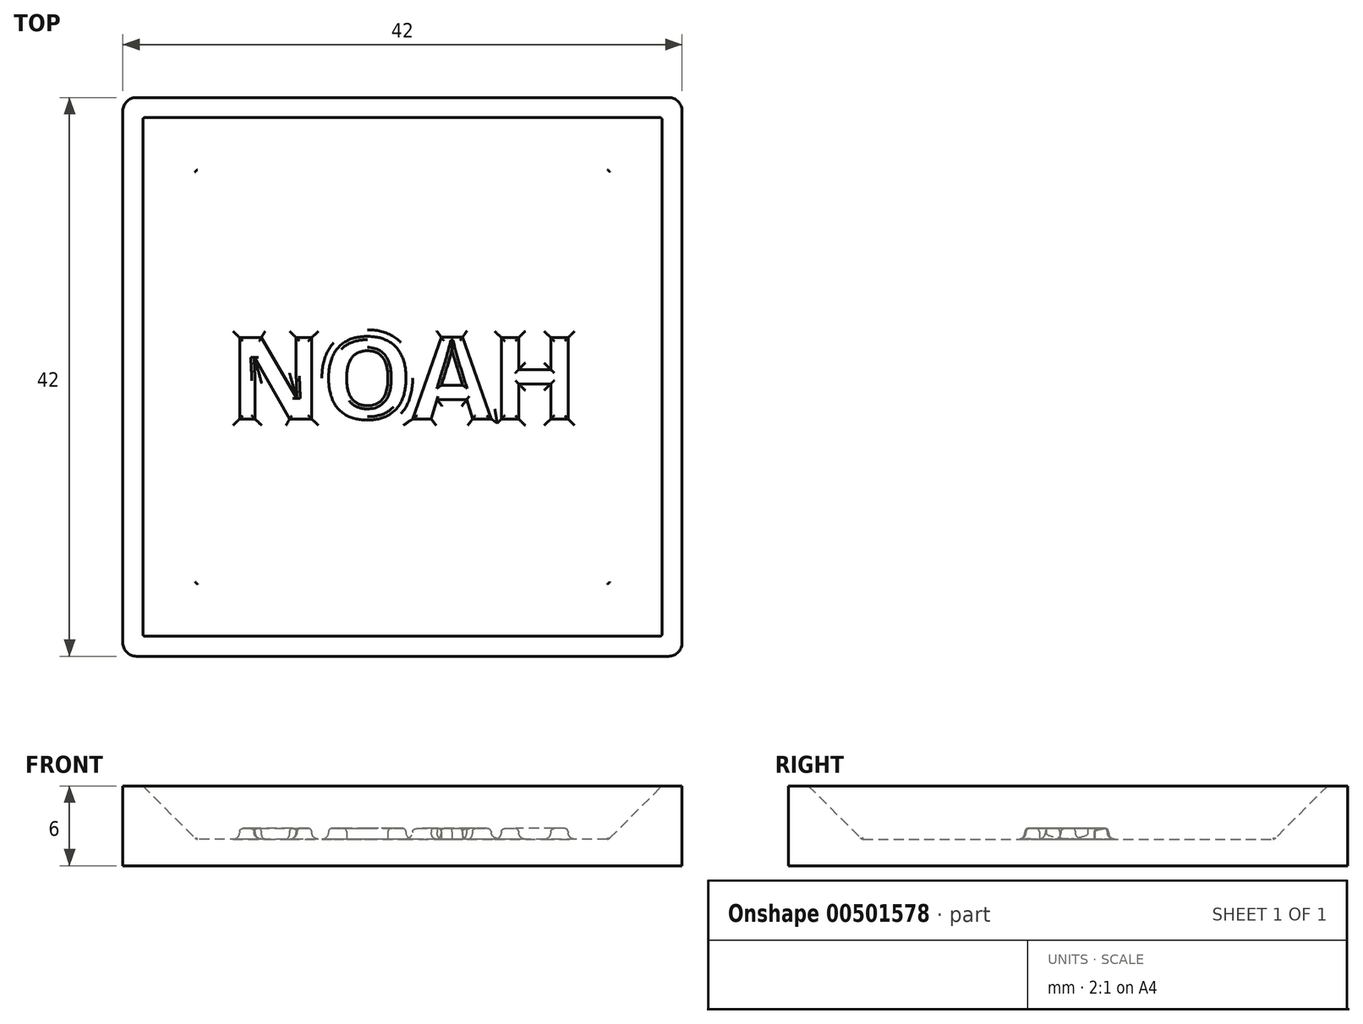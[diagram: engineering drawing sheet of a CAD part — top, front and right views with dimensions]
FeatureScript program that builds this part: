
annotation { "Feature Type Name" : "Feature", "Feature Type Description" : "" }
export const myFeature = defineFeature(function(context is Context, id is Id, definition is map)
    precondition{}
    {
        {
            var Q0;
            Q0=qCreatedBy(makeId("Top.planeOp"),FACE);
            var sketch = newSketch(context, id + "F0", { "sketchPlane" : qUnion([Q0])});
            skLineSegment(sketch, "E0.bottom", {"start": v(-21, 21) * mm, "end": v(21, 21) * mm});
            skLineSegment(sketch, "E0.top", {"start": v(-21, -21) * mm, "end": v(21, -21) * mm});
            skLineSegment(sketch, "E0.left", {"start": v(-21, 21) * mm, "end": v(-21, -21) * mm});
            skLineSegment(sketch, "E0.right", {"start": v(21, 21) * mm, "end": v(21, -21) * mm});
            skSolve(sketch);
        }
        {
            var Q0;
            Q0=qSketchRegion(id+"F0",true);
            extrude(context, id + "F1", {"entities" : qUnion([Q0]), "depth" : 2 * mm});
        }
        {
            var Q0;
            Q0=makeQuery(id+"F1.opExtrude","CAP_FACE",FACE,{"disambiguationData":[OSD([sQuery(id+"F0.wireOp",EDGE,"E0.bottom"),sQuery(id+"F0.wireOp",EDGE,"E0.top"),sQuery(id+"F0.wireOp",EDGE,"E0.left"),sQuery(id+"F0.wireOp",EDGE,"E0.right")])],"isStart":false});
            var sketch = newSketch(context, id + "F2", { "sketchPlane" : qUnion([Q0])});
            skLineSegment(sketch, "E1.bottom", {"start": v(-21, 21) * mm, "end": v(21, 21) * mm});
            skLineSegment(sketch, "E1.top", {"start": v(-21, -21) * mm, "end": v(21, -21) * mm});
            skLineSegment(sketch, "E1.left", {"start": v(-21, 21) * mm, "end": v(-21, -21) * mm});
            skLineSegment(sketch, "E1.right", {"start": v(21, 21) * mm, "end": v(21, -21) * mm});
            skLineSegment(sketch, "E2.bottom", {"start": v(-15.5, 15.5) * mm, "end": v(15.5, 15.5) * mm});
            skLineSegment(sketch, "E2.top", {"start": v(-15.5, -15.5) * mm, "end": v(15.5, -15.5) * mm});
            skLineSegment(sketch, "E2.left", {"start": v(-15.5, 15.5) * mm, "end": v(-15.5, -15.5) * mm});
            skLineSegment(sketch, "E2.right", {"start": v(15.5, 15.5) * mm, "end": v(15.5, -15.5) * mm});
            skSolve(sketch);
        }
        {
            var Q0;
            Q0=qSketchRegion(id+"F2",true);
            extrude(context, id + "F3", {"entities" : qUnion([Q0]), "operationType" : NewBodyOperationType.ADD, "depth" : 4 * mm});
        }
        {
            var Q0;
            Q0=makeQuery(id+"F3.opExtrude","CAP_EDGE",EDGE,{"disambiguationData":[OSD([sQuery(id+"F2.wireOp",EDGE,"E2.left")])],"isStart":false});
            var Q1;
            Q1=makeQuery(id+"F3.opExtrude","CAP_EDGE",EDGE,{"disambiguationData":[OSD([sQuery(id+"F2.wireOp",EDGE,"E2.bottom")])],"isStart":false});
            var Q2;
            Q2=makeQuery(id+"F3.opExtrude","CAP_EDGE",EDGE,{"disambiguationData":[OSD([sQuery(id+"F2.wireOp",EDGE,"E2.right")])],"isStart":false});
            var Q3;
            Q3=makeQuery(id+"F3.opExtrude","CAP_EDGE",EDGE,{"disambiguationData":[OSD([sQuery(id+"F2.wireOp",EDGE,"E2.top")])],"isStart":false});
            chamfer(context, id + "F4", {"entities" : qUnion([Q0, Q1, Q2, Q3]), "width" : 4 * mm, "tangentPropagation" : true});
        }
        {
            var Q0;
            Q0=makeQuery(id+"F1.opExtrude","CAP_FACE",FACE,{"disambiguationData":[OSD([sQuery(id+"F0.wireOp",EDGE,"E0.bottom"),sQuery(id+"F0.wireOp",EDGE,"E0.top"),sQuery(id+"F0.wireOp",EDGE,"E0.left"),sQuery(id+"F0.wireOp",EDGE,"E0.right")])],"isStart":false});
            var sketch = newSketch(context, id + "F5", { "sketchPlane" : qUnion([Q0])});
            skText(sketch, "E3", { "text": "NOAH", "fontName": "OpenSans-Bold.ttf"});
            const initialGuessF5  = {"E3": [-0.013, -0.00316, 1, 0, 0.00616]};
            skSetInitialGuess(sketch, initialGuessF5);
            skSolve(sketch);
        }
        {
            var Q0;
            Q0 = qSketchRegion(id + "F5", true);
            extrude(context, id + "F6", {"entities" : qUnion([Q0]), "operationType" : NewBodyOperationType.ADD, "depth" : .8 * mm, "offsetDistance" : 25 * mm});
        }
        {
            var Q0;
            Q0=makeQuery(id+"F6.opExtrude","CAP_EDGE",EDGE,{"disambiguationData":[OSD([sQuery(id+"F5.wireOp",EDGE,"E3.sketch_text.stroke-36")])],"isStart":false});
            var Q1;
            Q1=makeQuery(id+"F6.opExtrude","CAP_EDGE",EDGE,{"disambiguationData":[OSD([sQuery(id+"F5.wireOp",EDGE,"E3.sketch_text.stroke-38")])],"isStart":false});
            var Q2;
            Q2=makeQuery(id+"F6.opExtrude","CAP_EDGE",EDGE,{"disambiguationData":[OSD([sQuery(id+"F5.wireOp",EDGE,"E3.sketch_text.stroke-39")])],"isStart":false});
            var Q3;
            Q3=makeQuery(id+"F6.opExtrude","CAP_EDGE",EDGE,{"disambiguationData":[OSD([sQuery(id+"F5.wireOp",EDGE,"E3.sketch_text.stroke-29")])],"isStart":false});
            var Q4;
            Q4=makeQuery(id+"F6.opExtrude","CAP_EDGE",EDGE,{"disambiguationData":[OSD([sQuery(id+"F5.wireOp",EDGE,"E3.sketch_text.stroke-28")])],"isStart":false});
            var Q5;
            Q5=makeQuery(id+"F6.opExtrude","CAP_EDGE",EDGE,{"disambiguationData":[OSD([sQuery(id+"F5.wireOp",EDGE,"E3.sketch_text.stroke-35")])],"isStart":false});
            var Q6;
            Q6=makeQuery(id+"F6.opExtrude","CAP_EDGE",EDGE,{"disambiguationData":[OSD([sQuery(id+"F5.wireOp",EDGE,"E3.sketch_text.stroke-34")])],"isStart":false});
            var Q7;
            Q7=makeQuery(id+"F6.opExtrude","CAP_EDGE",EDGE,{"disambiguationData":[OSD([sQuery(id+"F5.wireOp",EDGE,"E3.sketch_text.stroke-33")])],"isStart":false});
            var Q8;
            Q8=makeQuery(id+"F6.opExtrude","CAP_EDGE",EDGE,{"disambiguationData":[OSD([sQuery(id+"F5.wireOp",EDGE,"E3.sketch_text.stroke-32")])],"isStart":false});
            var Q9;
            Q9=makeQuery(id+"F6.opExtrude","CAP_EDGE",EDGE,{"disambiguationData":[OSD([sQuery(id+"F5.wireOp",EDGE,"E3.sketch_text.stroke-31")])],"isStart":false});
            var Q10;
            Q10=makeQuery(id+"F6.opExtrude","CAP_EDGE",EDGE,{"disambiguationData":[OSD([sQuery(id+"F5.wireOp",EDGE,"E3.sketch_text.stroke-45")])],"isStart":false});
            var Q11;
            Q11=makeQuery(id+"F6.opExtrude","CAP_EDGE",EDGE,{"disambiguationData":[OSD([sQuery(id+"F5.wireOp",EDGE,"E3.sketch_text.stroke-44")])],"isStart":false});
            var Q12;
            Q12=makeQuery(id+"F6.opExtrude","CAP_EDGE",EDGE,{"disambiguationData":[OSD([sQuery(id+"F5.wireOp",EDGE,"E3.sketch_text.stroke-43")])],"isStart":false});
            var Q13;
            Q13=makeQuery(id+"F6.opExtrude","CAP_EDGE",EDGE,{"disambiguationData":[OSD([sQuery(id+"F5.wireOp",EDGE,"E3.sketch_text.stroke-42")])],"isStart":false});
            var Q14;
            Q14=makeQuery(id+"F6.opExtrude","CAP_EDGE",EDGE,{"disambiguationData":[OSD([sQuery(id+"F5.wireOp",EDGE,"E3.sketch_text.stroke-41")])],"isStart":false});
            var Q15;
            Q15=makeQuery(id+"F6.opExtrude","CAP_EDGE",EDGE,{"disambiguationData":[OSD([sQuery(id+"F5.wireOp",EDGE,"E3.sketch_text.stroke-40")])],"isStart":false});
            var Q16;
            Q16=makeQuery(id+"F6.opExtrude","CAP_EDGE",EDGE,{"disambiguationData":[OSD([sQuery(id+"F5.wireOp",EDGE,"E3.sketch_text.stroke-51")])],"isStart":false});
            var Q17;
            Q17=makeQuery(id+"F6.opExtrude","CAP_EDGE",EDGE,{"disambiguationData":[OSD([sQuery(id+"F5.wireOp",EDGE,"E3.sketch_text.stroke-50")])],"isStart":false});
            var Q18;
            Q18=makeQuery(id+"F6.opExtrude","CAP_EDGE",EDGE,{"disambiguationData":[OSD([sQuery(id+"F5.wireOp",EDGE,"E3.sketch_text.stroke-49")])],"isStart":false});
            var Q19;
            Q19=makeQuery(id+"F6.opExtrude","CAP_EDGE",EDGE,{"disambiguationData":[OSD([sQuery(id+"F5.wireOp",EDGE,"E3.sketch_text.stroke-48")])],"isStart":false});
            var Q20;
            Q20=makeQuery(id+"F6.opExtrude","CAP_EDGE",EDGE,{"disambiguationData":[OSD([sQuery(id+"F5.wireOp",EDGE,"E3.sketch_text.stroke-47")])],"isStart":false});
            var Q21;
            Q21=makeQuery(id+"F6.opExtrude","CAP_EDGE",EDGE,{"disambiguationData":[OSD([sQuery(id+"F5.wireOp",EDGE,"E3.sketch_text.stroke-46")])],"isStart":false});
            var Q22;
            Q22=makeQuery(id+"F6.opExtrude","CAP_EDGE",EDGE,{"disambiguationData":[OSD([sQuery(id+"F5.wireOp",EDGE,"E3.sketch_text.stroke-16")])],"isStart":false});
            var Q23;
            Q23=makeQuery(id+"F6.opExtrude","CAP_EDGE",EDGE,{"disambiguationData":[OSD([sQuery(id+"F5.wireOp",EDGE,"E3.sketch_text.stroke-25")])],"isStart":false});
            var Q24;
            Q24=makeQuery(id+"F6.opExtrude","CAP_EDGE",EDGE,{"disambiguationData":[OSD([sQuery(id+"F5.wireOp",EDGE,"E3.sketch_text.stroke-13")])],"isStart":false});
            var Q25;
            Q25=makeQuery(id+"F6.opExtrude","CAP_EDGE",EDGE,{"disambiguationData":[OSD([sQuery(id+"F5.wireOp",EDGE,"E3.sketch_text.stroke-12")])],"isStart":false});
            var Q26;
            Q26=makeQuery(id+"F6.opExtrude","CAP_EDGE",EDGE,{"disambiguationData":[OSD([sQuery(id+"F5.wireOp",EDGE,"E3.sketch_text.stroke-11")])],"isStart":false});
            var Q27;
            Q27=makeQuery(id+"F6.opExtrude","CAP_EDGE",EDGE,{"disambiguationData":[OSD([sQuery(id+"F5.wireOp",EDGE,"E3.sketch_text.stroke-8")])],"isStart":false});
            var Q28;
            Q28=makeQuery(id+"F6.opExtrude","CAP_EDGE",EDGE,{"disambiguationData":[OSD([sQuery(id+"F5.wireOp",EDGE,"E3.sketch_text.stroke-7")])],"isStart":false});
            var Q29;
            Q29=makeQuery(id+"F6.opExtrude","CAP_EDGE",EDGE,{"disambiguationData":[OSD([sQuery(id+"F5.wireOp",EDGE,"E3.sketch_text.stroke-6")])],"isStart":false});
            var Q30;
            Q30=makeQuery(id+"F6.opExtrude","CAP_EDGE",EDGE,{"disambiguationData":[OSD([sQuery(id+"F5.wireOp",EDGE,"E3.sketch_text.stroke-5")])],"isStart":false});
            var Q31;
            Q31=makeQuery(id+"F6.opExtrude","CAP_EDGE",EDGE,{"disambiguationData":[OSD([sQuery(id+"F5.wireOp",EDGE,"E3.sketch_text.stroke-4")])],"isStart":false});
            var Q32;
            Q32=makeQuery(id+"F6.opExtrude","CAP_EDGE",EDGE,{"disambiguationData":[OSD([sQuery(id+"F5.wireOp",EDGE,"E3.sketch_text.stroke-1")])],"isStart":false});
            var Q33;
            Q33=makeQuery(id+"F6.opExtrude","CAP_EDGE",EDGE,{"disambiguationData":[OSD([sQuery(id+"F5.wireOp",EDGE,"E3.sketch_text.stroke-0")])],"isStart":false});
            fillet(context, id + "F7", {"entities" : qUnion([Q0, Q1, Q2, Q3, Q4, Q5, Q6, Q7, Q8, Q9, Q10, Q11, Q12, Q13, Q14, Q15, Q16, Q17, Q18, Q19, Q20, Q21, Q22, Q23, Q24, Q25, Q26, Q27, Q28, Q29, Q30, Q31, Q32, Q33]), "radius" : .25 * mm, "tangentPropagation" : true, "allowEdgeOverflow" : false});
        }
        {
            var Q0;
            Q0=makeQuery(id+"F6.opExtrude","CAP_EDGE",EDGE,{"disambiguationData":[OSD([sQuery(id+"F5.wireOp",EDGE,"E3.sketch_text.stroke-5")])],"isStart":true});
            var Q1;
            Q1=makeQuery(id+"F6.opExtrude","CAP_EDGE",EDGE,{"disambiguationData":[OSD([sQuery(id+"F5.wireOp",EDGE,"E3.sketch_text.stroke-4")])],"isStart":true});
            var Q2;
            Q2=makeQuery(id+"F6.opExtrude","CAP_EDGE",EDGE,{"disambiguationData":[OSD([sQuery(id+"F5.wireOp",EDGE,"E3.sketch_text.stroke-1")])],"isStart":true});
            var Q3;
            Q3=makeQuery(id+"F6.opExtrude","CAP_EDGE",EDGE,{"disambiguationData":[OSD([sQuery(id+"F5.wireOp",EDGE,"E3.sketch_text.stroke-0")])],"isStart":true});
            var Q4;
            Q4=makeQuery(id+"F6.opExtrude","CAP_EDGE",EDGE,{"disambiguationData":[OSD([sQuery(id+"F5.wireOp",EDGE,"E3.sketch_text.stroke-13")])],"isStart":true});
            var Q5;
            Q5=makeQuery(id+"F6.opExtrude","CAP_EDGE",EDGE,{"disambiguationData":[OSD([sQuery(id+"F5.wireOp",EDGE,"E3.sketch_text.stroke-12")])],"isStart":true});
            var Q6;
            Q6=makeQuery(id+"F6.opExtrude","CAP_EDGE",EDGE,{"disambiguationData":[OSD([sQuery(id+"F5.wireOp",EDGE,"E3.sketch_text.stroke-11")])],"isStart":true});
            var Q7;
            Q7=makeQuery(id+"F6.opExtrude","CAP_EDGE",EDGE,{"disambiguationData":[OSD([sQuery(id+"F5.wireOp",EDGE,"E3.sketch_text.stroke-8")])],"isStart":true});
            var Q8;
            Q8=makeQuery(id+"F6.opExtrude","CAP_EDGE",EDGE,{"disambiguationData":[OSD([sQuery(id+"F5.wireOp",EDGE,"E3.sketch_text.stroke-7")])],"isStart":true});
            var Q9;
            Q9=makeQuery(id+"F6.opExtrude","CAP_EDGE",EDGE,{"disambiguationData":[OSD([sQuery(id+"F5.wireOp",EDGE,"E3.sketch_text.stroke-6")])],"isStart":true});
            var Q10;
            Q10=makeQuery(id+"F6.opExtrude","CAP_EDGE",EDGE,{"disambiguationData":[OSD([sQuery(id+"F5.wireOp",EDGE,"E3.sketch_text.stroke-16")])],"isStart":true});
            var Q11;
            Q11=makeQuery(id+"F6.opExtrude","CAP_EDGE",EDGE,{"disambiguationData":[OSD([sQuery(id+"F5.wireOp",EDGE,"E3.sketch_text.stroke-25")])],"isStart":true});
            var Q12;
            Q12=makeQuery(id+"F6.opExtrude","CAP_EDGE",EDGE,{"disambiguationData":[OSD([sQuery(id+"F5.wireOp",EDGE,"E3.sketch_text.stroke-32")])],"isStart":true});
            var Q13;
            Q13=makeQuery(id+"F6.opExtrude","CAP_EDGE",EDGE,{"disambiguationData":[OSD([sQuery(id+"F5.wireOp",EDGE,"E3.sketch_text.stroke-31")])],"isStart":true});
            var Q14;
            Q14=makeQuery(id+"F6.opExtrude","CAP_EDGE",EDGE,{"disambiguationData":[OSD([sQuery(id+"F5.wireOp",EDGE,"E3.sketch_text.stroke-30")])],"isStart":true});
            var Q15;
            Q15=makeQuery(id+"F6.opExtrude","CAP_EDGE",EDGE,{"disambiguationData":[OSD([sQuery(id+"F5.wireOp",EDGE,"E3.sketch_text.stroke-29")])],"isStart":true});
            var Q16;
            Q16=makeQuery(id+"F6.opExtrude","CAP_EDGE",EDGE,{"disambiguationData":[OSD([sQuery(id+"F5.wireOp",EDGE,"E3.sketch_text.stroke-28")])],"isStart":true});
            var Q17;
            Q17=makeQuery(id+"F6.opExtrude","CAP_EDGE",EDGE,{"disambiguationData":[OSD([sQuery(id+"F5.wireOp",EDGE,"E3.sketch_text.stroke-35")])],"isStart":true});
            var Q18;
            Q18=makeQuery(id+"F6.opExtrude","CAP_EDGE",EDGE,{"disambiguationData":[OSD([sQuery(id+"F5.wireOp",EDGE,"E3.sketch_text.stroke-34")])],"isStart":true});
            var Q19;
            Q19=makeQuery(id+"F6.opExtrude","CAP_EDGE",EDGE,{"disambiguationData":[OSD([sQuery(id+"F5.wireOp",EDGE,"E3.sketch_text.stroke-33")])],"isStart":true});
            var Q20;
            Q20=makeQuery(id+"F6.opExtrude","CAP_EDGE",EDGE,{"disambiguationData":[OSD([sQuery(id+"F5.wireOp",EDGE,"E3.sketch_text.stroke-45")])],"isStart":true});
            var Q21;
            Q21=makeQuery(id+"F6.opExtrude","CAP_EDGE",EDGE,{"disambiguationData":[OSD([sQuery(id+"F5.wireOp",EDGE,"E3.sketch_text.stroke-44")])],"isStart":true});
            var Q22;
            Q22=makeQuery(id+"F6.opExtrude","CAP_EDGE",EDGE,{"disambiguationData":[OSD([sQuery(id+"F5.wireOp",EDGE,"E3.sketch_text.stroke-43")])],"isStart":true});
            var Q23;
            Q23=makeQuery(id+"F6.opExtrude","CAP_EDGE",EDGE,{"disambiguationData":[OSD([sQuery(id+"F5.wireOp",EDGE,"E3.sketch_text.stroke-42")])],"isStart":true});
            var Q24;
            Q24=makeQuery(id+"F6.opExtrude","CAP_EDGE",EDGE,{"disambiguationData":[OSD([sQuery(id+"F5.wireOp",EDGE,"E3.sketch_text.stroke-41")])],"isStart":true});
            var Q25;
            Q25=makeQuery(id+"F6.opExtrude","CAP_EDGE",EDGE,{"disambiguationData":[OSD([sQuery(id+"F5.wireOp",EDGE,"E3.sketch_text.stroke-40")])],"isStart":true});
            var Q26;
            Q26=makeQuery(id+"F6.opExtrude","CAP_EDGE",EDGE,{"disambiguationData":[OSD([sQuery(id+"F5.wireOp",EDGE,"E3.sketch_text.stroke-51")])],"isStart":true});
            var Q27;
            Q27=makeQuery(id+"F6.opExtrude","CAP_EDGE",EDGE,{"disambiguationData":[OSD([sQuery(id+"F5.wireOp",EDGE,"E3.sketch_text.stroke-50")])],"isStart":true});
            var Q28;
            Q28=makeQuery(id+"F6.opExtrude","CAP_EDGE",EDGE,{"disambiguationData":[OSD([sQuery(id+"F5.wireOp",EDGE,"E3.sketch_text.stroke-49")])],"isStart":true});
            var Q29;
            Q29=makeQuery(id+"F6.opExtrude","CAP_EDGE",EDGE,{"disambiguationData":[OSD([sQuery(id+"F5.wireOp",EDGE,"E3.sketch_text.stroke-48")])],"isStart":true});
            var Q30;
            Q30=makeQuery(id+"F6.opExtrude","CAP_EDGE",EDGE,{"disambiguationData":[OSD([sQuery(id+"F5.wireOp",EDGE,"E3.sketch_text.stroke-47")])],"isStart":true});
            var Q31;
            Q31=makeQuery(id+"F6.opExtrude","CAP_EDGE",EDGE,{"disambiguationData":[OSD([sQuery(id+"F5.wireOp",EDGE,"E3.sketch_text.stroke-46")])],"isStart":true});
            fillet(context, id + "F8", {"entities" : qUnion([Q0, Q1, Q2, Q3, Q4, Q5, Q6, Q7, Q8, Q9, Q10, Q11, Q12, Q13, Q14, Q15, Q16, Q17, Q18, Q19, Q20, Q21, Q22, Q23, Q24, Q25, Q26, Q27, Q28, Q29, Q30, Q31]), "radius" : .5 * mm, "tangentPropagation" : true, "allowEdgeOverflow" : false});
        }
        {
            var Q0;
            Q0=makeQuery(id+"F3.boolean.opBoolean","MERGE",EDGE,{"derivedFrom":[makeQuery(id+"F1.opExtrude","SWEPT_EDGE",EDGE,{"disambiguationData":[OSD([sQuery(id+"F0.wireOp",EDGE,"E0.top"),sQuery(id+"F0.wireOp",EDGE,"E0.right")])]}),makeQuery(id+"F3.opExtrude","SWEPT_EDGE",EDGE,{"disambiguationData":[OSD([sQuery(id+"F2.wireOp",EDGE,"E1.top"),sQuery(id+"F2.wireOp",EDGE,"E1.right")])]})]});
            var Q1;
            Q1=makeQuery(id+"F3.boolean.opBoolean","MERGE",EDGE,{"derivedFrom":[makeQuery(id+"F1.opExtrude","SWEPT_EDGE",EDGE,{"disambiguationData":[OSD([sQuery(id+"F0.wireOp",EDGE,"E0.bottom"),sQuery(id+"F0.wireOp",EDGE,"E0.right")])]}),makeQuery(id+"F3.opExtrude","SWEPT_EDGE",EDGE,{"disambiguationData":[OSD([sQuery(id+"F2.wireOp",EDGE,"E1.bottom"),sQuery(id+"F2.wireOp",EDGE,"E1.right")])]})]});
            var Q2;
            Q2=makeQuery(id+"F3.boolean.opBoolean","MERGE",EDGE,{"derivedFrom":[makeQuery(id+"F1.opExtrude","SWEPT_EDGE",EDGE,{"disambiguationData":[OSD([sQuery(id+"F0.wireOp",EDGE,"E0.bottom"),sQuery(id+"F0.wireOp",EDGE,"E0.left")])]}),makeQuery(id+"F3.opExtrude","SWEPT_EDGE",EDGE,{"disambiguationData":[OSD([sQuery(id+"F2.wireOp",EDGE,"E1.bottom"),sQuery(id+"F2.wireOp",EDGE,"E1.left")])]})]});
            var Q3;
            Q3=makeQuery(id+"F3.boolean.opBoolean","MERGE",EDGE,{"derivedFrom":[makeQuery(id+"F1.opExtrude","SWEPT_EDGE",EDGE,{"disambiguationData":[OSD([sQuery(id+"F0.wireOp",EDGE,"E0.top"),sQuery(id+"F0.wireOp",EDGE,"E0.left")])]}),makeQuery(id+"F3.opExtrude","SWEPT_EDGE",EDGE,{"disambiguationData":[OSD([sQuery(id+"F2.wireOp",EDGE,"E1.top"),sQuery(id+"F2.wireOp",EDGE,"E1.left")])]})]});
            fillet(context, id + "F9", {"entities" : qUnion([Q0, Q1, Q2, Q3]), "radius" : 1 * mm, "tangentPropagation" : true, "allowEdgeOverflow" : false});
        }
        {
            var Q0;
            Q0=makeQuery(id+"F4.opChamfer","BLEND_EDGE",EDGE,{"blendedFrom":[makeQuery(id+"F3.opExtrude","CAP_EDGE",EDGE,{"disambiguationData":[OSD([sQuery(id+"F2.wireOp",EDGE,"E2.left")])],"isStart":false}),makeQuery(id+"F1.opExtrude","CAP_FACE",FACE,{"disambiguationData":[OSD([sQuery(id+"F0.wireOp",EDGE,"E0.bottom"),sQuery(id+"F0.wireOp",EDGE,"E0.top"),sQuery(id+"F0.wireOp",EDGE,"E0.left"),sQuery(id+"F0.wireOp",EDGE,"E0.right")])],"isStart":false})],"blendedInto":[makeQuery(id+"F1.opExtrude","CAP_FACE",FACE,{"disambiguationData":[OSD([sQuery(id+"F0.wireOp",EDGE,"E0.bottom"),sQuery(id+"F0.wireOp",EDGE,"E0.top"),sQuery(id+"F0.wireOp",EDGE,"E0.left"),sQuery(id+"F0.wireOp",EDGE,"E0.right")])],"isStart":false})]});
            var Q1;
            Q1=makeQuery(id+"F4.opChamfer","BLEND_EDGE",EDGE,{"blendedFrom":[makeQuery(id+"F3.opExtrude","CAP_EDGE",EDGE,{"disambiguationData":[OSD([sQuery(id+"F2.wireOp",EDGE,"E2.bottom")])],"isStart":false}),makeQuery(id+"F1.opExtrude","CAP_FACE",FACE,{"disambiguationData":[OSD([sQuery(id+"F0.wireOp",EDGE,"E0.bottom"),sQuery(id+"F0.wireOp",EDGE,"E0.top"),sQuery(id+"F0.wireOp",EDGE,"E0.left"),sQuery(id+"F0.wireOp",EDGE,"E0.right")])],"isStart":false})],"blendedInto":[makeQuery(id+"F1.opExtrude","CAP_FACE",FACE,{"disambiguationData":[OSD([sQuery(id+"F0.wireOp",EDGE,"E0.bottom"),sQuery(id+"F0.wireOp",EDGE,"E0.top"),sQuery(id+"F0.wireOp",EDGE,"E0.left"),sQuery(id+"F0.wireOp",EDGE,"E0.right")])],"isStart":false})]});
            var Q2;
            Q2=makeQuery(id+"F4.opChamfer","BLEND_EDGE",EDGE,{"blendedFrom":[makeQuery(id+"F3.opExtrude","CAP_EDGE",EDGE,{"disambiguationData":[OSD([sQuery(id+"F2.wireOp",EDGE,"E2.right")])],"isStart":false}),makeQuery(id+"F1.opExtrude","CAP_FACE",FACE,{"disambiguationData":[OSD([sQuery(id+"F0.wireOp",EDGE,"E0.bottom"),sQuery(id+"F0.wireOp",EDGE,"E0.top"),sQuery(id+"F0.wireOp",EDGE,"E0.left"),sQuery(id+"F0.wireOp",EDGE,"E0.right")])],"isStart":false})],"blendedInto":[makeQuery(id+"F1.opExtrude","CAP_FACE",FACE,{"disambiguationData":[OSD([sQuery(id+"F0.wireOp",EDGE,"E0.bottom"),sQuery(id+"F0.wireOp",EDGE,"E0.top"),sQuery(id+"F0.wireOp",EDGE,"E0.left"),sQuery(id+"F0.wireOp",EDGE,"E0.right")])],"isStart":false})]});
            var Q3;
            Q3=makeQuery(id+"F4.opChamfer","BLEND_EDGE",EDGE,{"blendedFrom":[makeQuery(id+"F3.opExtrude","CAP_EDGE",EDGE,{"disambiguationData":[OSD([sQuery(id+"F2.wireOp",EDGE,"E2.top")])],"isStart":false}),makeQuery(id+"F1.opExtrude","CAP_FACE",FACE,{"disambiguationData":[OSD([sQuery(id+"F0.wireOp",EDGE,"E0.bottom"),sQuery(id+"F0.wireOp",EDGE,"E0.top"),sQuery(id+"F0.wireOp",EDGE,"E0.left"),sQuery(id+"F0.wireOp",EDGE,"E0.right")])],"isStart":false})],"blendedInto":[makeQuery(id+"F1.opExtrude","CAP_FACE",FACE,{"disambiguationData":[OSD([sQuery(id+"F0.wireOp",EDGE,"E0.bottom"),sQuery(id+"F0.wireOp",EDGE,"E0.top"),sQuery(id+"F0.wireOp",EDGE,"E0.left"),sQuery(id+"F0.wireOp",EDGE,"E0.right")])],"isStart":false})]});
            var Q4;
            Q4=makeQuery(id+"F4.opChamfer","BLEND_EDGE",EDGE,{"blendedFrom":[makeQuery(id+"F3.opExtrude","CAP_EDGE",EDGE,{"disambiguationData":[OSD([sQuery(id+"F2.wireOp",EDGE,"E2.bottom")])],"isStart":false}),makeQuery(id+"F3.opExtrude","CAP_EDGE",EDGE,{"disambiguationData":[OSD([sQuery(id+"F2.wireOp",EDGE,"E2.right")])],"isStart":false})],"blendedInto":[]});
            var Q5;
            Q5=makeQuery(id+"F4.opChamfer","BLEND_EDGE",EDGE,{"blendedFrom":[makeQuery(id+"F3.opExtrude","CAP_EDGE",EDGE,{"disambiguationData":[OSD([sQuery(id+"F2.wireOp",EDGE,"E2.bottom")])],"isStart":false}),makeQuery(id+"F3.opExtrude","CAP_EDGE",EDGE,{"disambiguationData":[OSD([sQuery(id+"F2.wireOp",EDGE,"E2.left")])],"isStart":false})],"blendedInto":[]});
            var Q6;
            Q6=makeQuery(id+"F4.opChamfer","BLEND_EDGE",EDGE,{"blendedFrom":[makeQuery(id+"F3.opExtrude","CAP_EDGE",EDGE,{"disambiguationData":[OSD([sQuery(id+"F2.wireOp",EDGE,"E2.top")])],"isStart":false}),makeQuery(id+"F3.opExtrude","CAP_EDGE",EDGE,{"disambiguationData":[OSD([sQuery(id+"F2.wireOp",EDGE,"E2.left")])],"isStart":false})],"blendedInto":[]});
            var Q7;
            Q7=makeQuery(id+"F4.opChamfer","BLEND_EDGE",EDGE,{"blendedFrom":[makeQuery(id+"F3.opExtrude","CAP_EDGE",EDGE,{"disambiguationData":[OSD([sQuery(id+"F2.wireOp",EDGE,"E2.top")])],"isStart":false}),makeQuery(id+"F3.opExtrude","CAP_EDGE",EDGE,{"disambiguationData":[OSD([sQuery(id+"F2.wireOp",EDGE,"E2.right")])],"isStart":false})],"blendedInto":[]});
            fillet(context, id + "F10", {"entities" : qUnion([Q0, Q1, Q2, Q3, Q4, Q5, Q6, Q7]), "radius" : .25 * mm, "tangentPropagation" : true, "allowEdgeOverflow" : false});
        }
    });
